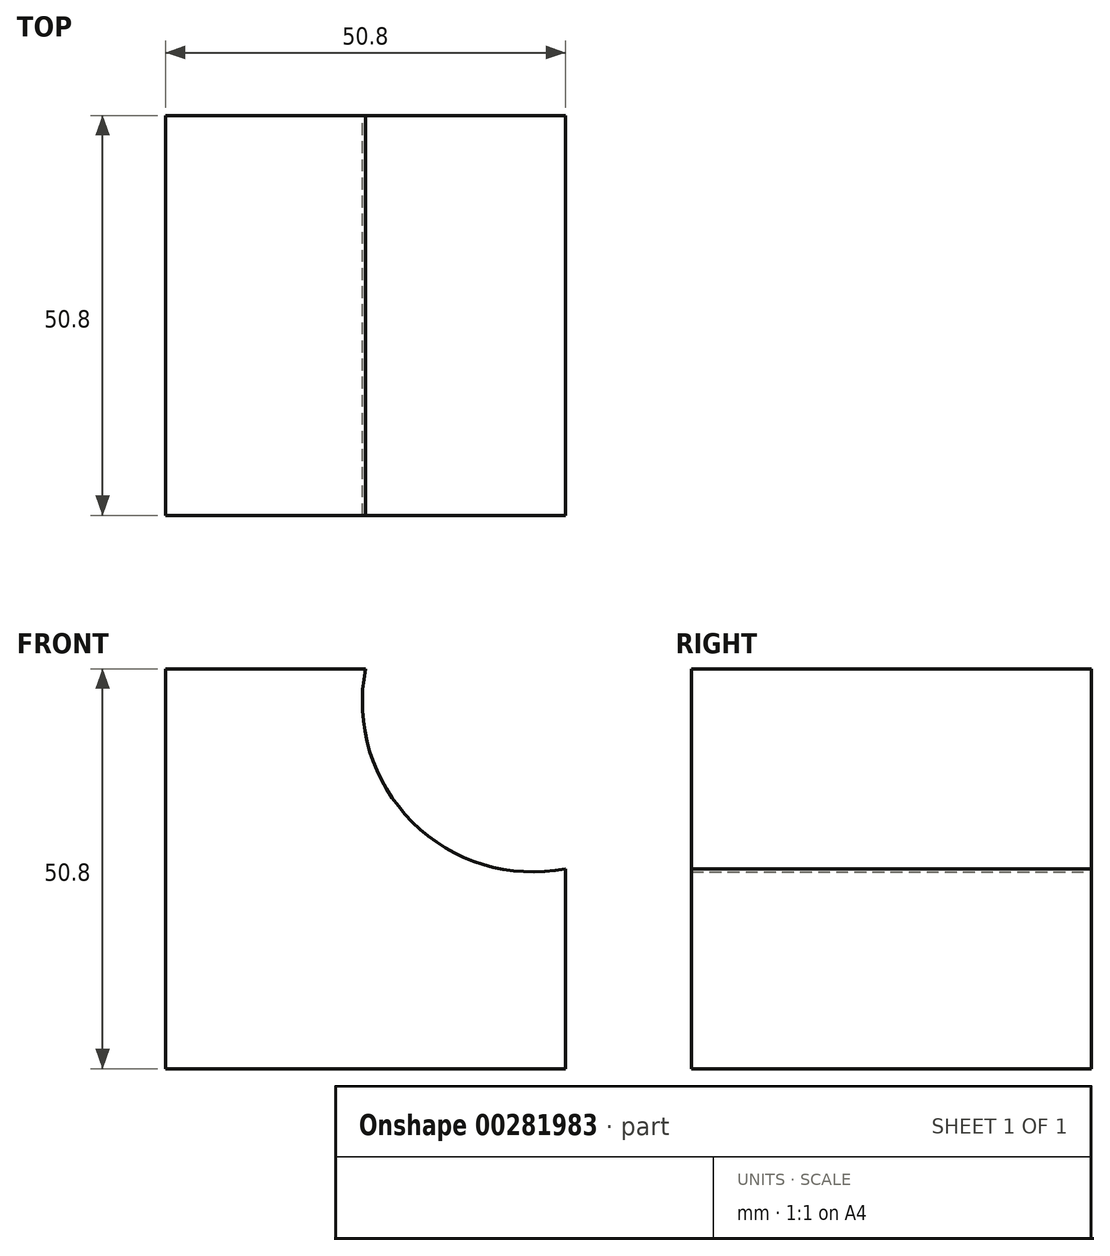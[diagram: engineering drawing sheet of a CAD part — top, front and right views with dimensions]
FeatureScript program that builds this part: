
annotation { "Feature Type Name" : "Feature", "Feature Type Description" : "" }
export const myFeature = defineFeature(function(context is Context, id is Id, definition is map)
    precondition{}
    {
        {
            var Q0;
            Q0=qCreatedBy(makeId("Front.planeOp"),FACE);
            var sketch = newSketch(context, id + "F0", { "sketchPlane" : qUnion([Q0])});
            skLineSegment(sketch, "E0", {"start": v(0, 0) * mm, "end": v(-50.8, 0) * mm});
            skLineSegment(sketch, "E1", {"start": v(-50.8, 0) * mm, "end": v(-50.8, 50.8) * mm});
            skLineSegment(sketch, "E2", {"start": v(-50.8, 50.8) * mm, "end": v(-25.4, 50.8) * mm});
            skLineSegment(sketch, "E3", {"start": v(0, 0) * mm, "end": v(0, 25.4) * mm});
            skArc(sketch, "E4", {"start": v(-25.4, 50.8) * mm, "mid": v(-19.47, 31.33) * mm, "end": v(0, 25.4) * mm});
            skSolve(sketch);
        }
        {
            var Q0;
            Q0 = qSketchRegion(id + "F0", true);
            extrude(context, id + "F1", {"entities" : qUnion([Q0]), "depth" : 50.8 * mm});
        }
    });
